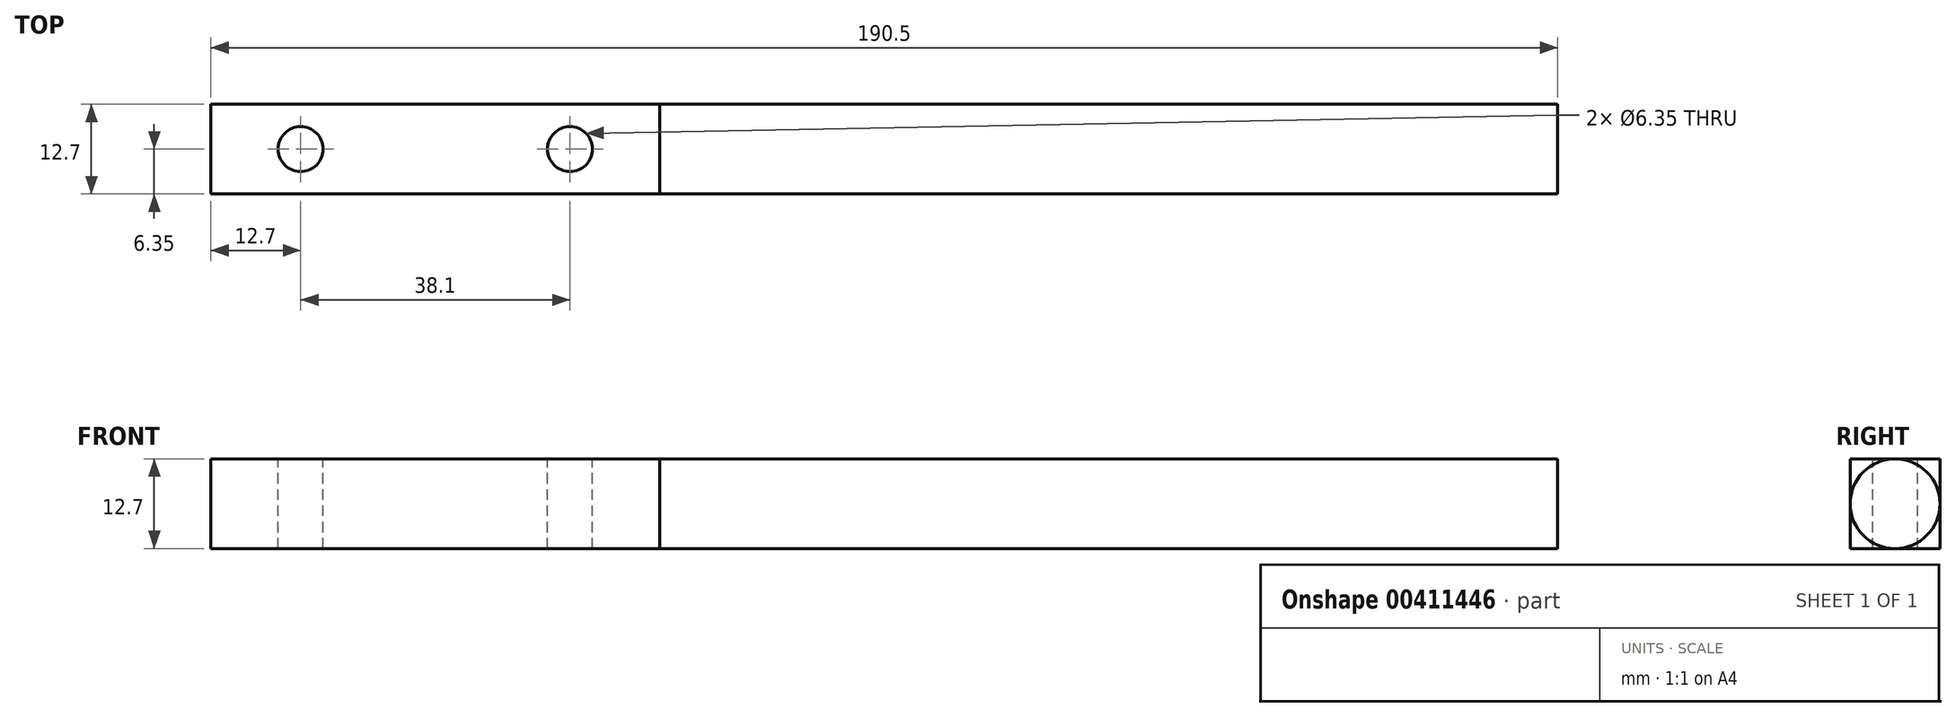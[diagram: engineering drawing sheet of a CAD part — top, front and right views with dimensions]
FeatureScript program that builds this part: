
annotation { "Feature Type Name" : "Feature", "Feature Type Description" : "" }
export const myFeature = defineFeature(function(context is Context, id is Id, definition is map)
    precondition{}
    {
        {
            var Q0;
            Q0=qCreatedBy(makeId("Right.planeOp"),FACE);
            var sketch = newSketch(context, id + "F0", { "sketchPlane" : qUnion([Q0])});
            skLineSegment(sketch, "E0.bottom", {"start": v(0, 0) * mm, "end": v(12.7, 0) * mm});
            skLineSegment(sketch, "E0.top", {"start": v(0, 12.7) * mm, "end": v(12.7, 12.7) * mm});
            skLineSegment(sketch, "E0.left", {"start": v(0, 0) * mm, "end": v(0, 12.7) * mm});
            skLineSegment(sketch, "E0.right", {"start": v(12.7, 0) * mm, "end": v(12.7, 12.7) * mm});
            skSolve(sketch);
        }
        {
            var Q0;
            Q0 = qSketchRegion(id + "F0", true);
            extrude(context, id + "F1", {"entities" : qUnion([Q0]), "depth" : 63.5 * mm});
        }
        {
            var Q0;
            Q0=makeQuery(id+"F1.opExtrude","CAP_FACE",FACE,{"disambiguationData":[OSD([sQuery(id+"F0.wireOp",EDGE,"E0.bottom"),sQuery(id+"F0.wireOp",EDGE,"E0.top"),sQuery(id+"F0.wireOp",EDGE,"E0.left"),sQuery(id+"F0.wireOp",EDGE,"E0.right")])],"isStart":false});
            var sketch = newSketch(context, id + "F2", { "sketchPlane" : qUnion([Q0])});
            skCircle(sketch, "E1", {"center": v(6.35, 6.35) * mm, "radius": 6.35 * mm});
            skSolve(sketch);
        }
        {
            var Q0;
            Q0 = qSketchRegion(id + "F2", true);
            extrude(context, id + "F3", {"entities" : qUnion([Q0]), "operationType" : NewBodyOperationType.ADD, "depth" : 127 * mm});
        }
        {
            var Q0;
            Q0=makeQuery(id+"F1.opExtrude","SWEPT_FACE",FACE,{"disambiguationData":[OSD([sQuery(id+"F0.wireOp",EDGE,"E0.top")])]});
            var sketch = newSketch(context, id + "F4", { "sketchPlane" : qUnion([Q0])});
            skCircle(sketch, "E2", {"center": v(12.7, 6.35) * mm, "radius": 3.18 * mm});
            skCircle(sketch, "E3", {"center": v(50.8, 6.35) * mm, "radius": 3.18 * mm});
            skSolve(sketch);
        }
        {
            var Q0;
            Q0 = qSketchRegion(id + "F4", true);
            extrude(context, id + "F5", {"entities" : qUnion([Q0]), "operationType" : NewBodyOperationType.REMOVE, "oppositeDirection" : true, "depth" : 25.4 * mm});
        }
    });
